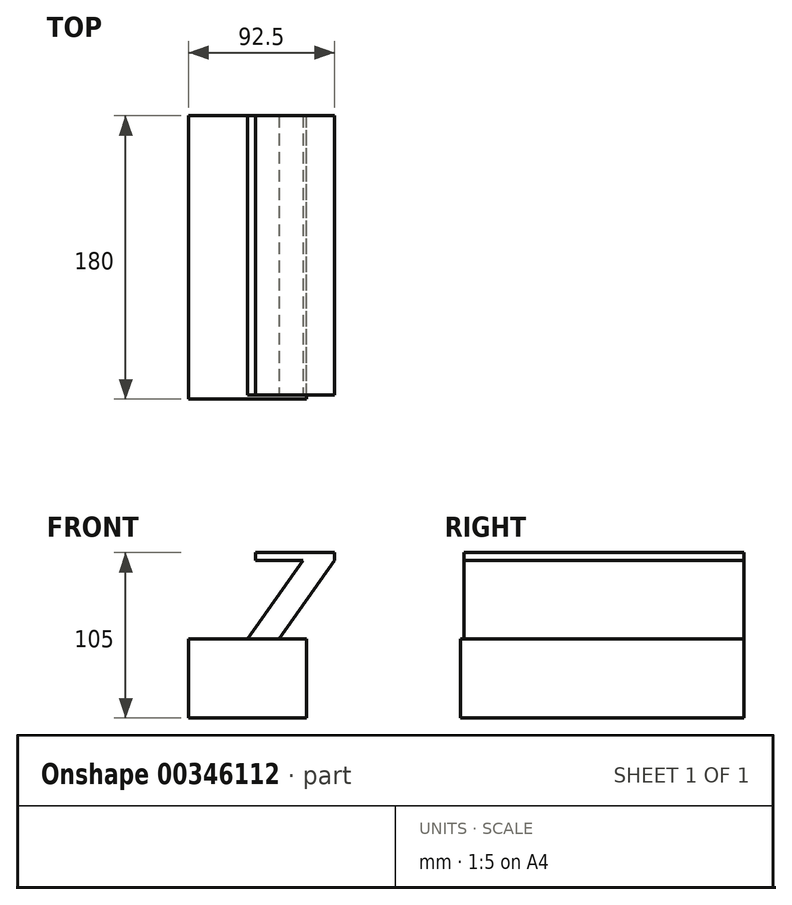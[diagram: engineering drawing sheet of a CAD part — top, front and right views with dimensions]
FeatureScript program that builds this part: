
annotation { "Feature Type Name" : "Feature", "Feature Type Description" : "" }
export const myFeature = defineFeature(function(context is Context, id is Id, definition is map)
    precondition{}
    {
        {
            var Q0;
            Q0=qCreatedBy(makeId("Top.planeOp"),FACE);
            var sketch = newSketch(context, id + "F0", { "sketchPlane" : qUnion([Q0])});
            skLineSegment(sketch, "E0.bottom", {"start": v(-200, 0) * mm, "end": v(-125, 0) * mm});
            skLineSegment(sketch, "E0.top", {"start": v(-200, 180) * mm, "end": v(-125, 180) * mm});
            skLineSegment(sketch, "E0.left", {"start": v(-200, 0) * mm, "end": v(-200, 180) * mm});
            skLineSegment(sketch, "E0.right", {"start": v(-125, 0) * mm, "end": v(-125, 180) * mm});
            skSolve(sketch);
        }
        {
            var Q0;
            Q0 = qSketchRegion(id + "F0", true);
            extrude(context, id + "F1", {"entities" : qUnion([Q0]), "depth" : 50 * mm});
        }
        {
            var Q0;
            Q0=makeQuery(id+"F1.opExtrude","CAP_FACE",FACE,{"disambiguationData":[OSD([sQuery(id+"F0.wireOp",EDGE,"E0.bottom"),sQuery(id+"F0.wireOp",EDGE,"E0.top"),sQuery(id+"F0.wireOp",EDGE,"E0.left"),sQuery(id+"F0.wireOp",EDGE,"E0.right")])],"isStart":false});
            var sketch = newSketch(context, id + "F2", { "sketchPlane" : qUnion([Q0])});
            skLineSegment(sketch, "E1", {"start": v(-162.5, 180) * mm, "end": v(-162.5, 50) * mm});
            skLineSegment(sketch, "E2.bottom", {"start": v(-162.5, 180) * mm, "end": v(-147.5, 180) * mm});
            skLineSegment(sketch, "E2.top", {"start": v(-162.5, 50) * mm, "end": v(-147.5, 50) * mm});
            skLineSegment(sketch, "E2.right", {"start": v(-147.5, 180) * mm, "end": v(-147.5, 50) * mm});
            skSolve(sketch);
        }
        {
            var Q0;
            Q0=makeQuery(id+"F2.imprint","IMPRINT",FACE,{"disambiguationData":[TD([[makeQuery(id+"F2.imprint","IMPRINT",EDGE,{"derivedFrom":sQuery(id+"F2.wireOp",EDGE,"E2.bottom")}),-1.0]])]});
            extrude(context, id + "F3", {"entities" : qUnion([Q0]), "operationType" : NewBodyOperationType.ADD, "depth" : 50 * mm});
        }
        {
            var Q0;
            Q0=makeQuery(id+"F3.opExtrude","SWEPT_FACE",FACE,{"disambiguationData":[OSD([sQuery(id+"F2.wireOp",EDGE,"E2.right")])]});
            extrude(context, id + "F4", {"entities" : qUnion([Q0]), "operationType" : NewBodyOperationType.ADD, "depth" : 40 * mm});
        }
        {
            var Q0;
            {var subQ0=sQuery(id+"F2.wireOp",EDGE,"E2.top");Q0=makeQuery(id+"F4.boolean.opBoolean","MERGE",FACE,{"derivedFrom":[makeQuery(id+"F3.opExtrude","SWEPT_FACE",FACE,{"disambiguationData":[OSD([subQ0])]}),makeQuery(id+"F4.opExtrude","SWEPT_FACE",FACE,{"disambiguationData":[OSD([subQ0,sQuery(id+"F2.wireOp",EDGE,"E2.right")])]})]});}
            var sketch = newSketch(context, id + "F5", { "sketchPlane" : qUnion([Q0])});
            skLineSegment(sketch, "E3", {"start": v(-107.5, 50) * mm, "end": v(-142.5, 50) * mm});
            skLineSegment(sketch, "E4", {"start": v(-162.5, 100) * mm, "end": v(-127.5, 100) * mm});
            skLineSegment(sketch, "E5", {"start": v(-162.5, 50) * mm, "end": v(-127.5, 100) * mm});
            skLineSegment(sketch, "E6", {"start": v(-142.5, 50) * mm, "end": v(-107.5, 100) * mm});
            skLineSegment(sketch, "E7", {"start": v(-107.5, 50) * mm, "end": v(-125, 50) * mm});
            skSolve(sketch);
        }
        {
            var Q0;
            Q0=makeQuery(id+"F5.imprint","IMPRINT",FACE,{"disambiguationData":[TD([[makeQuery(id+"F5.imprint","IMPRINT",EDGE,{"derivedFrom":sQuery(id+"F5.wireOp",EDGE,"E4")}),-1.0]])]});
            var Q1;
            {var subQ5=sQuery(id+"F5.wireOp",EDGE,"E6");Q1=makeQuery(id+"F5.imprint","IMPRINT",FACE,{"disambiguationData":[TD([[makeQuery(id+"F5.imprint","IMPRINT",EDGE,{"derivedFrom":subQ5}),-1.0]])]});}
            extrude(context, id + "F6", {"entities" : qUnion([Q0, Q1]), "operationType" : NewBodyOperationType.REMOVE, "oppositeDirection" : true, "depth" : 200 * mm});
        }
        {
            var Q0;
            {var subQ0=sQuery(id+"F2.wireOp",EDGE,"E2.right");Q0=makeQuery(id+"F4.boolean.opBoolean","MERGE",FACE,{"derivedFrom":[makeQuery(id+"F3.opExtrude","CAP_FACE",FACE,{"disambiguationData":[OSD([sQuery(id+"F2.wireOp",EDGE,"E2.bottom"),sQuery(id+"F2.wireOp",EDGE,"E2.top"),sQuery(id+"F2.wireOp",EDGE,"E1"),subQ0])],"isStart":false}),makeQuery(id+"F4.opExtrude","SWEPT_FACE",FACE,{"disambiguationData":[OSD([subQ0]),TDD([makeQuery(id+"F3.opExtrude","CAP_EDGE",EDGE,{"disambiguationData":[OSD([subQ0])],"isStart":false})])]})]});}
            extrude(context, id + "F7", {"entities" : qUnion([Q0]), "operationType" : NewBodyOperationType.ADD, "depth" : 5 * mm});
        }
        {
            var Q0;
            Q0=makeQuery(id+"F7.opExtrude","SWEPT_FACE",FACE,{"disambiguationData":[OSD([sQuery(id+"F2.wireOp",EDGE,"E2.top"),sQuery(id+"F2.wireOp",EDGE,"E2.right"),sQuery(id+"F5.wireOp",EDGE,"E4"),sQuery(id+"F5.wireOp",EDGE,"E5")])]});
            extrude(context, id + "F8", {"entities" : qUnion([Q0]), "operationType" : NewBodyOperationType.ADD, "depth" : 40 * mm});
        }
        {
            var Q0;
            {var subQ0=sQuery(id+"F5.wireOp",EDGE,"E5");var subQ1=sQuery(id+"F5.wireOp",EDGE,"E4");var subQ2=sQuery(id+"F2.wireOp",EDGE,"E2.right");var subQ3=sQuery(id+"F2.wireOp",EDGE,"E2.top");Q0=makeQuery(id+"F8.boolean.opBoolean","MERGE",FACE,{"derivedFrom":[makeQuery(id+"F7.boolean.opBoolean","MERGE",FACE,{"derivedFrom":[makeQuery(id+"F4.boolean.opBoolean","MERGE",FACE,{"derivedFrom":[makeQuery(id+"F3.opExtrude","SWEPT_FACE",FACE,{"disambiguationData":[OSD([subQ3])]}),makeQuery(id+"F4.opExtrude","SWEPT_FACE",FACE,{"disambiguationData":[OSD([subQ3,subQ2])]})]}),makeQuery(id+"F7.opExtrude","SWEPT_FACE",FACE,{"disambiguationData":[OSD([subQ3,subQ2])]})]}),makeQuery(id+"F8.opExtrude","SWEPT_FACE",FACE,{"disambiguationData":[OSD([subQ3,subQ2,subQ1,subQ0]),TDD([makeQuery(id+"F7.opExtrude","SWEPT_EDGE",EDGE,{"disambiguationData":[OSD([subQ3,subQ2,subQ1,subQ0])]})])]})]});}
            var sketch = newSketch(context, id + "F9", { "sketchPlane" : qUnion([Q0])});
            skLineSegment(sketch, "E8", {"start": v(-127.5, 100) * mm, "end": v(-107.5, 100) * mm});
            skSolve(sketch);
        }
        {
            var Q0;
            Q0=makeQuery(id+"F9.imprint","IMPRINT",FACE,{"disambiguationData":[TD([[makeQuery(id+"F9.imprint","IMPRINT",EDGE,{"derivedFrom":sQuery(id+"F9.wireOp",EDGE,"E8")}),1.0]])]});
            extrude(context, id + "F10", {"entities" : qUnion([Q0]), "operationType" : NewBodyOperationType.ADD, "depth" : 30 * mm});
        }
        {
            var Q0;
            {var subQ0=sQuery(id+"F5.wireOp",EDGE,"E6");var subQ1=sQuery(id+"F2.wireOp",EDGE,"E2.right");var subQ2=sQuery(id+"F2.wireOp",EDGE,"E2.top");Q0=makeQuery(id+"F10.boolean.opBoolean","MERGE",FACE,{"derivedFrom":[makeQuery(id+"F7.opExtrude","SWEPT_FACE",FACE,{"disambiguationData":[OSD([subQ2,subQ1,subQ0])]}),makeQuery(id+"F10.opExtrude","SWEPT_FACE",FACE,{"disambiguationData":[OSD([subQ2,subQ1,subQ0])]})]});}
            extrude(context, id + "F11", {"entities" : qUnion([Q0]), "operationType" : NewBodyOperationType.ADD, "depth" : 7.5 * mm});
        }
    });
